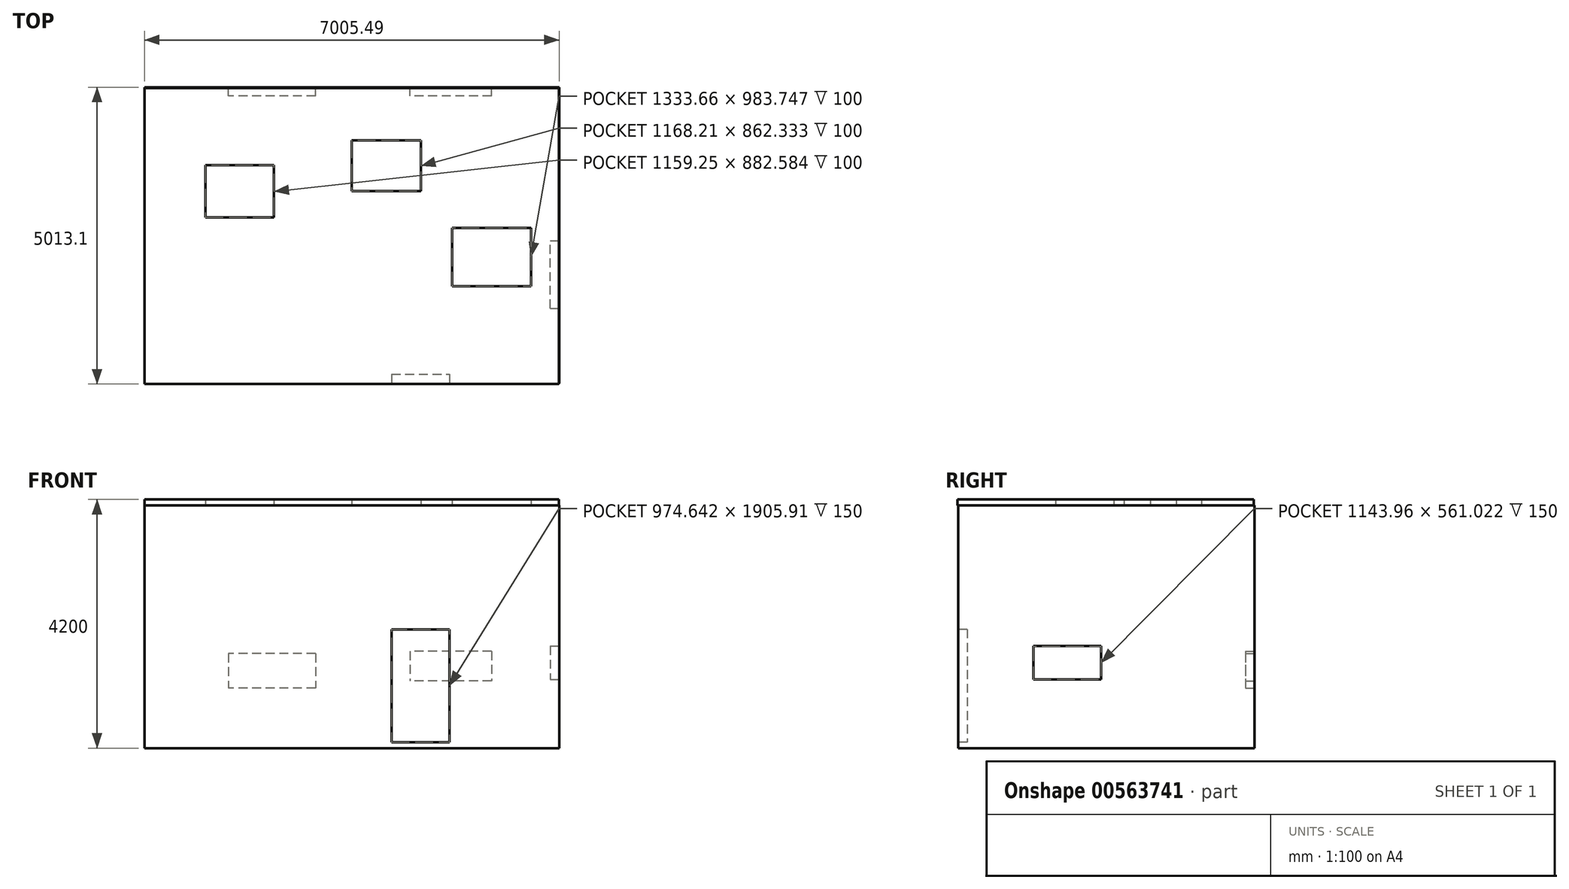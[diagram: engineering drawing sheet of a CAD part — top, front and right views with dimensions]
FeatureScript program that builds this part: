
annotation { "Feature Type Name" : "Feature", "Feature Type Description" : "" }
export const myFeature = defineFeature(function(context is Context, id is Id, definition is map)
    precondition{}
    {
        {
            var Q0;
            Q0=qCreatedBy(makeId("Top.planeOp"),FACE);
            var sketch = newSketch(context, id + "F0", { "sketchPlane" : qUnion([Q0])});
            skLineSegment(sketch, "E0.bottom", {"start": v(-3494.68, 2786.29) * mm, "end": v(3505.32, 2786.29) * mm});
            skLineSegment(sketch, "E0.top", {"start": v(-3494.68, -2213.71) * mm, "end": v(3505.32, -2213.71) * mm});
            skLineSegment(sketch, "E0.left", {"start": v(-3494.68, 2786.29) * mm, "end": v(-3494.68, -2213.71) * mm});
            skLineSegment(sketch, "E0.right", {"start": v(3505.32, 2786.29) * mm, "end": v(3505.32, -2213.71) * mm});
            skSolve(sketch);
        }
        {
            var Q0;
            Q0=qSketchRegion(id+"F0",true);
            extrude(context, id + "F1", {"entities" : qUnion([Q0]), "depth" : 4100 * mm, "offsetDistance" : 25.4 * mm});
        }
        {
            var Q0;
            Q0=makeQuery(id+"F1.opExtrude","CAP_VERTEX",VERTEX,{"disambiguationData":[OSD([sQuery(id+"F0.wireOp",EDGE,"E0.bottom"),sQuery(id+"F0.wireOp",EDGE,"E0.left")])],"isStart":false});
            var Q1;
            Q1=makeQuery(id+"F1.opExtrude","CAP_VERTEX",VERTEX,{"disambiguationData":[OSD([sQuery(id+"F0.wireOp",EDGE,"E0.bottom"),sQuery(id+"F0.wireOp",EDGE,"E0.right")])],"isStart":false});
            var Q2;
            Q2=makeQuery(id+"F1.opExtrude","CAP_VERTEX",VERTEX,{"disambiguationData":[OSD([sQuery(id+"F0.wireOp",EDGE,"E0.top"),sQuery(id+"F0.wireOp",EDGE,"E0.left")])],"isStart":false});
            cPlane(context, id + "F2", {"entities" : qUnion([Q0, Q1, Q2]), "cplaneType" : CPlaneType.THREE_POINT, "offset" : 25.4 * mm, "width" : 152.4 * mm, "height" : 152.4 * mm});
        }
        {
            var Q0;
            Q0=qCreatedBy(id+"F2.planeOp",FACE);
            var sketch = newSketch(context, id + "F3", { "sketchPlane" : qUnion([Q0])});
            skLineSegment(sketch, "E1.bottom", {"start": v(3501.6, 2774.45) * mm, "end": v(-3500.17, 2774.45) * mm});
            skLineSegment(sketch, "E1.top", {"start": v(3501.6, -2226.81) * mm, "end": v(-3500.17, -2226.81) * mm});
            skLineSegment(sketch, "E1.left", {"start": v(3501.6, 2774.45) * mm, "end": v(3501.6, -2226.81) * mm});
            skLineSegment(sketch, "E1.right", {"start": v(-3500.17, 2774.45) * mm, "end": v(-3500.17, -2226.81) * mm});
            skSolve(sketch);
        }
        {
            var Q0;
            Q0=qSketchRegion(id+"F3",true);
            extrude(context, id + "F4", {"entities" : qUnion([Q0]), "operationType" : NewBodyOperationType.ADD, "depth" : 100 * mm, "offsetDistance" : 25.4 * mm});
        }
        {
            var Q0;
            Q0=qCreatedBy(id+"F2.planeOp",FACE);
            var sketch = newSketch(context, id + "F5", { "sketchPlane" : qUnion([Q0])});
            skLineSegment(sketch, "E2.bottom", {"start": v(-1310.33, 1466.9) * mm, "end": v(-2469.58, 1466.9) * mm});
            skLineSegment(sketch, "E2.top", {"start": v(-1310.33, 584.32) * mm, "end": v(-2469.58, 584.32) * mm});
            skLineSegment(sketch, "E2.left", {"start": v(-1310.33, 1466.9) * mm, "end": v(-1310.33, 584.32) * mm});
            skLineSegment(sketch, "E2.right", {"start": v(-2469.58, 1466.9) * mm, "end": v(-2469.58, 584.32) * mm});
            skLineSegment(sketch, "E3.bottom", {"start": v(1168.21, 1890.78) * mm, "end": v(0, 1890.78) * mm});
            skLineSegment(sketch, "E3.top", {"start": v(1168.21, 1028.45) * mm, "end": v(0, 1028.45) * mm});
            skLineSegment(sketch, "E3.left", {"start": v(1168.21, 1890.78) * mm, "end": v(1168.21, 1028.45) * mm});
            skLineSegment(sketch, "E3.right", {"start": v(0, 1890.78) * mm, "end": v(0, 1028.45) * mm});
            skLineSegment(sketch, "E4.bottom", {"start": v(3033.42, 410.39) * mm, "end": v(1699.76, 410.39) * mm});
            skLineSegment(sketch, "E4.top", {"start": v(3033.42, -573.36) * mm, "end": v(1699.76, -573.36) * mm});
            skLineSegment(sketch, "E4.left", {"start": v(3033.42, 410.39) * mm, "end": v(3033.42, -573.36) * mm});
            skLineSegment(sketch, "E4.right", {"start": v(1699.76, 410.39) * mm, "end": v(1699.76, -573.36) * mm});
            skSolve(sketch);
        }
        {
            var Q0;
            Q0=qSketchRegion(id+"F5",true);
            extrude(context, id + "F6", {"entities" : qUnion([Q0]), "operationType" : NewBodyOperationType.REMOVE, "depth" : 150 * mm, "offsetDistance" : 25.4 * mm});
        }
        {
            var Q0;
            Q0=makeQuery(id+"F1.opExtrude","SWEPT_FACE",FACE,{"disambiguationData":[OSD([sQuery(id+"F0.wireOp",EDGE,"E0.right")])]});
            var sketch = newSketch(context, id + "F7", { "sketchPlane" : qUnion([Q0])});
            skLineSegment(sketch, "E5.bottom", {"start": v(-947.88, 1721.58) * mm, "end": v(196.08, 1721.58) * mm});
            skLineSegment(sketch, "E5.top", {"start": v(-947.88, 1160.56) * mm, "end": v(196.08, 1160.56) * mm});
            skLineSegment(sketch, "E5.left", {"start": v(-947.88, 1721.58) * mm, "end": v(-947.88, 1160.56) * mm});
            skLineSegment(sketch, "E5.right", {"start": v(196.08, 1721.58) * mm, "end": v(196.08, 1160.56) * mm});
            skSolve(sketch);
        }
        {
            var Q0;
            Q0=makeQuery(id+"F7.imprint","IMPRINT",FACE,{"disambiguationData":[TD([[makeQuery(id+"F7.imprint","IMPRINT",EDGE,{"derivedFrom":sQuery(id+"F7.wireOp",EDGE,"E5.bottom")}),-1.0]])]});
            extrude(context, id + "F8", {"entities" : qUnion([Q0]), "operationType" : NewBodyOperationType.REMOVE, "oppositeDirection" : true, "depth" : 150 * mm, "offsetDistance" : 25.4 * mm});
        }
        {
            var Q0;
            Q0=makeQuery(id+"F1.opExtrude","SWEPT_FACE",FACE,{"disambiguationData":[OSD([sQuery(id+"F0.wireOp",EDGE,"E0.bottom")])]});
            var sketch = newSketch(context, id + "F9", { "sketchPlane" : qUnion([Q0])});
            skLineSegment(sketch, "E6.bottom", {"start": v(-2362.98, 1635.16) * mm, "end": v(-984.74, 1635.16) * mm});
            skLineSegment(sketch, "E6.top", {"start": v(-2362.98, 1133.92) * mm, "end": v(-984.74, 1133.92) * mm});
            skLineSegment(sketch, "E6.left", {"start": v(-2362.98, 1635.16) * mm, "end": v(-2362.98, 1133.92) * mm});
            skLineSegment(sketch, "E6.right", {"start": v(-984.74, 1635.16) * mm, "end": v(-984.74, 1133.92) * mm});
            skLineSegment(sketch, "E7.bottom", {"start": v(610.16, 1597.12) * mm, "end": v(2084.38, 1597.12) * mm});
            skLineSegment(sketch, "E7.top", {"start": v(610.16, 1015.37) * mm, "end": v(2084.38, 1015.37) * mm});
            skLineSegment(sketch, "E7.left", {"start": v(610.16, 1597.12) * mm, "end": v(610.16, 1015.37) * mm});
            skLineSegment(sketch, "E7.right", {"start": v(2084.38, 1597.12) * mm, "end": v(2084.38, 1015.37) * mm});
            skSolve(sketch);
        }
        {
            var Q0;
            Q0=qSketchRegion(id+"F9",true);
            extrude(context, id + "F10", {"entities" : qUnion([Q0]), "operationType" : NewBodyOperationType.REMOVE, "oppositeDirection" : true, "depth" : 150 * mm, "offsetDistance" : 25.4 * mm});
        }
        {
            var Q0;
            Q0=makeQuery(id+"F1.opExtrude","SWEPT_FACE",FACE,{"disambiguationData":[OSD([sQuery(id+"F0.wireOp",EDGE,"E0.top")])]});
            var sketch = newSketch(context, id + "F11", { "sketchPlane" : qUnion([Q0])});
            skLineSegment(sketch, "E8.bottom", {"start": v(675.87, 2005.91) * mm, "end": v(1650.5, 2005.91) * mm});
            skLineSegment(sketch, "E8.top", {"start": v(675.87, 100) * mm, "end": v(1650.5, 100) * mm});
            skLineSegment(sketch, "E8.left", {"start": v(675.87, 2005.91) * mm, "end": v(675.87, 100) * mm});
            skLineSegment(sketch, "E8.right", {"start": v(1650.5, 2005.91) * mm, "end": v(1650.5, 100) * mm});
            skSolve(sketch);
        }
        {
            var Q0;
            Q0=qSketchRegion(id+"F11",true);
            extrude(context, id + "F12", {"entities" : qUnion([Q0]), "operationType" : NewBodyOperationType.REMOVE, "oppositeDirection" : true, "depth" : 150 * mm, "offsetDistance" : 25.4 * mm});
        }
    });
